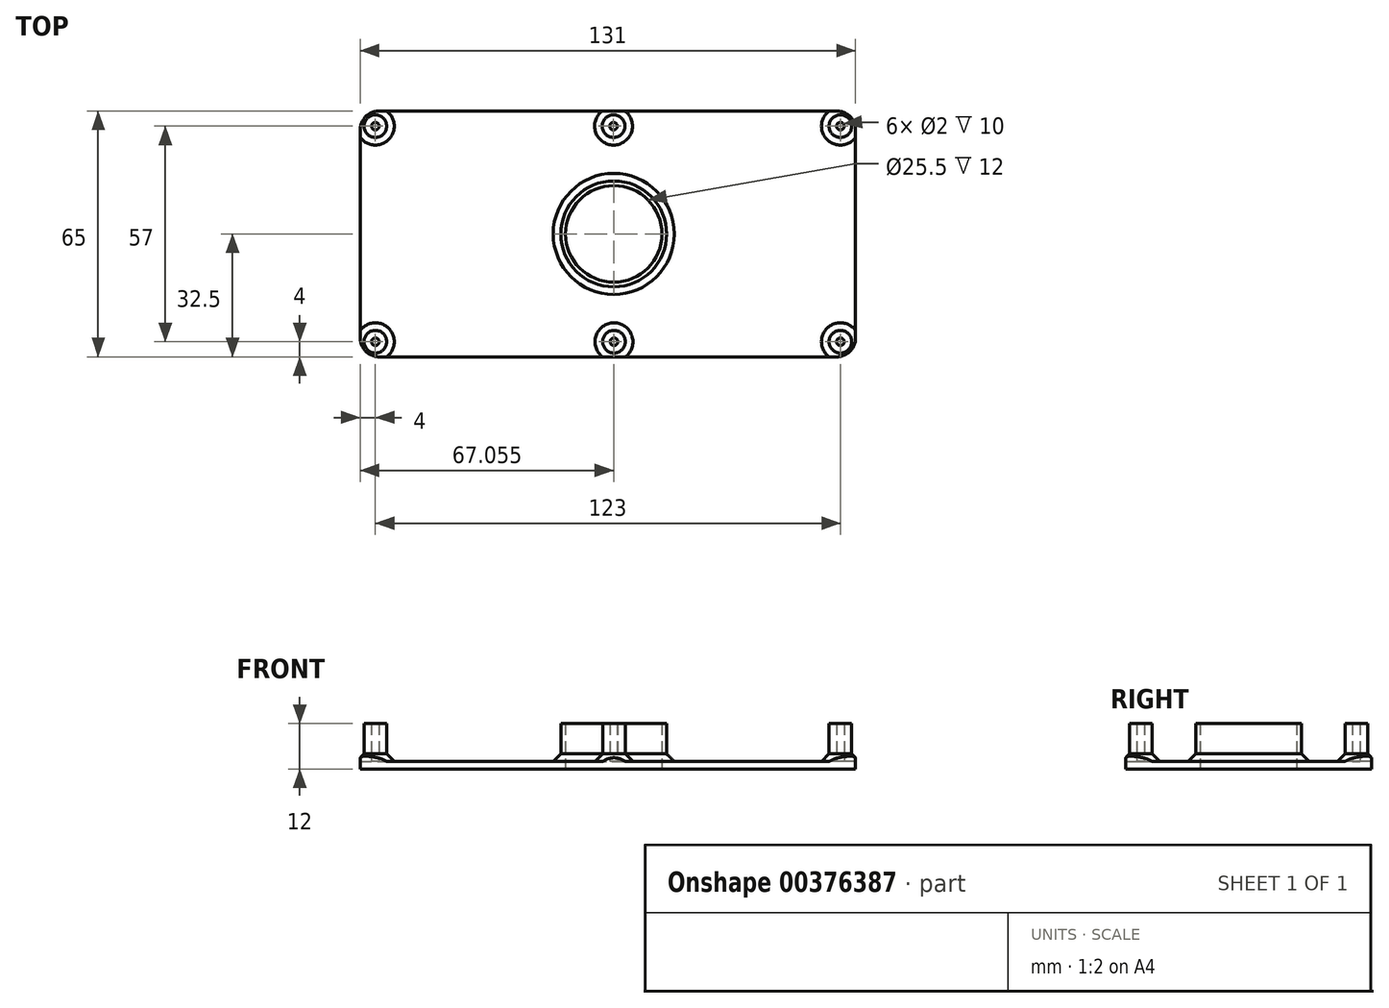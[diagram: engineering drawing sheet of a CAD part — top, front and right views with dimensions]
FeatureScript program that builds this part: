
annotation { "Feature Type Name" : "Feature", "Feature Type Description" : "" }
export const myFeature = defineFeature(function(context is Context, id is Id, definition is map)
    precondition{}
    {
        {
            var Q0;
            Q0=qCreatedBy(makeId("Top.planeOp"),FACE);
            var sketch = newSketch(context, id + "F0", { "sketchPlane" : qUnion([Q0])});
            skLineSegment(sketch, "E0.bottom", {"start": v(-65.5, 32.5) * mm, "end": v(65.5, 32.5) * mm});
            skLineSegment(sketch, "E0.top", {"start": v(-65.5, -32.5) * mm, "end": v(65.5, -32.5) * mm});
            skLineSegment(sketch, "E0.left", {"start": v(-65.5, 32.5) * mm, "end": v(-65.5, -32.5) * mm});
            skLineSegment(sketch, "E0.right", {"start": v(65.5, 32.5) * mm, "end": v(65.5, -32.5) * mm});
            skPoint(sketch, "E0.middle", {"position": v(0, 0) * mm});
            skLineSegment(sketch, "E1.bottom", {"start": v(-65.5, 32.5) * mm, "end": v(-61.5, 32.5) * mm, "construction": true});
            skLineSegment(sketch, "E1.top", {"start": v(-65.5, 28.5) * mm, "end": v(-61.5, 28.5) * mm, "construction": true});
            skLineSegment(sketch, "E1.left", {"start": v(-65.5, 32.5) * mm, "end": v(-65.5, 28.5) * mm, "construction": true});
            skLineSegment(sketch, "E1.right", {"start": v(-61.5, 32.5) * mm, "end": v(-61.5, 28.5) * mm, "construction": true});
            skLineSegment(sketch, "E2.bottom", {"start": v(65.5, 32.5) * mm, "end": v(61.5, 32.5) * mm, "construction": true});
            skLineSegment(sketch, "E2.top", {"start": v(65.5, 28.5) * mm, "end": v(61.5, 28.5) * mm, "construction": true});
            skLineSegment(sketch, "E2.left", {"start": v(65.5, 32.5) * mm, "end": v(65.5, 28.5) * mm, "construction": true});
            skLineSegment(sketch, "E2.right", {"start": v(61.5, 32.5) * mm, "end": v(61.5, 28.5) * mm, "construction": true});
            skLineSegment(sketch, "E3.bottom", {"start": v(-65.5, -32.5) * mm, "end": v(-61.5, -32.5) * mm, "construction": true});
            skLineSegment(sketch, "E3.top", {"start": v(-65.5, -28.5) * mm, "end": v(-61.5, -28.5) * mm, "construction": true});
            skLineSegment(sketch, "E3.left", {"start": v(-65.5, -32.5) * mm, "end": v(-65.5, -28.5) * mm, "construction": true});
            skLineSegment(sketch, "E3.right", {"start": v(-61.5, -32.5) * mm, "end": v(-61.5, -28.5) * mm, "construction": true});
            skLineSegment(sketch, "E4.bottom", {"start": v(65.5, -32.5) * mm, "end": v(61.5, -32.5) * mm, "construction": true});
            skLineSegment(sketch, "E4.top", {"start": v(65.5, -28.5) * mm, "end": v(61.5, -28.5) * mm, "construction": true});
            skLineSegment(sketch, "E4.left", {"start": v(65.5, -32.5) * mm, "end": v(65.5, -28.5) * mm, "construction": true});
            skLineSegment(sketch, "E4.right", {"start": v(61.5, -32.5) * mm, "end": v(61.5, -28.5) * mm, "construction": true});
            skCircle(sketch, "E5", {"center": v(-61.5, 28.5) * mm, "radius": 3 * mm});
            skCircle(sketch, "E6", {"center": v(-61.5, -28.5) * mm, "radius": 3 * mm});
            skCircle(sketch, "E7", {"center": v(61.5, -28.5) * mm, "radius": 3 * mm});
            skCircle(sketch, "E8", {"center": v(61.5, 28.5) * mm, "radius": 3 * mm});
            skLineSegment(sketch, "E9", {"start": v(65.5, 28.5) * mm, "end": v(1.5, 28.5) * mm, "construction": true});
            skPoint(sketch, "E9.endSnap0", {"position": v(63.5, 28.5) * mm});
            skLineSegment(sketch, "E10", {"start": v(65.5, -28.5) * mm, "end": v(1.61, -28.5) * mm});
            skLineSegment(sketch, "E11", {"start": v(1.5, 28.5) * mm, "end": v(1.5, 32.5) * mm, "construction": true});
            skLineSegment(sketch, "E12", {"start": v(1.61, -28.5) * mm, "end": v(1.61, -32.5) * mm, "construction": true});
            skCircle(sketch, "E13", {"center": v(1.5, 28.5) * mm, "radius": 3 * mm});
            skCircle(sketch, "E14", {"center": v(1.61, -28.5) * mm, "radius": 3 * mm});
            skLineSegment(sketch, "E15", {"start": v(1.5, 28.5) * mm, "end": v(1.61, -29.33) * mm, "construction": true});
            skCircle(sketch, "E16", {"center": v(1.55, 0) * mm, "radius": 14 * mm});
            skCircle(sketch, "E17", {"center": v(1.55, 0) * mm, "radius": 12.75 * mm});
            skSolve(sketch);
        }
        {
            var Q0;
            {var subQ7=sQuery(id+"F0.wireOp",EDGE,"E0.bottom");Q0=makeQuery(id+"F0.imprint","IMPRINT",FACE,{"disambiguationData":[TD([[makeQuery(id+"F0.imprint","IMPRINT",EDGE,{"derivedFrom":subQ7}),-1.0]])]});}
            var Q1;
            Q1=makeQuery(id+"F0.imprint","IMPRINT",FACE,{"disambiguationData":[TD([[makeQuery(id+"F0.imprint","IMPRINT",EDGE,{"derivedFrom":sQuery(id+"F0.wireOp",EDGE,"E13")}),1.0]])]});
            var Q2;
            Q2=makeQuery(id+"F0.imprint","IMPRINT",FACE,{"disambiguationData":[TD([[makeQuery(id+"F0.imprint","IMPRINT",EDGE,{"derivedFrom":sQuery(id+"F0.wireOp",EDGE,"E14")}),1.0]])]});
            var Q3;
            {var subQ0=sQuery(id+"F0.wireOp",EDGE,"E10");var subQ1=sQuery(id+"F0.wireOp",EDGE,"E7");var subQ2=makeQuery(id+"F0.imprint","INTERSECT",VERTEX,{"disambiguationData":[OD(0.0)],"derivedFrom":[subQ1,subQ0]});Q3=makeQuery(id+"F0.imprint","IMPRINT",FACE,{"disambiguationData":[TD([[makeQuery(id+"F0.imprint","IMPRINT",EDGE,{"disambiguationData":[TD([[subQ2,1.0]])],"derivedFrom":subQ1}),1.0]])]});}
            var Q4;
            {var subQ0=sQuery(id+"F0.wireOp",EDGE,"E10");var subQ1=sQuery(id+"F0.wireOp",EDGE,"E7");var subQ2=makeQuery(id+"F0.imprint","INTERSECT",VERTEX,{"disambiguationData":[OD(0.0)],"derivedFrom":[subQ1,subQ0]});Q4=makeQuery(id+"F0.imprint","IMPRINT",FACE,{"disambiguationData":[TD([[makeQuery(id+"F0.imprint","IMPRINT",EDGE,{"disambiguationData":[TD([[subQ2,-1.0]])],"derivedFrom":subQ1}),1.0]])]});}
            var Q5;
            Q5=makeQuery(id+"F0.imprint","IMPRINT",FACE,{"disambiguationData":[TD([[makeQuery(id+"F0.imprint","IMPRINT",EDGE,{"derivedFrom":sQuery(id+"F0.wireOp",EDGE,"E8")}),1.0]])]});
            var Q6;
            Q6=makeQuery(id+"F0.imprint","IMPRINT",FACE,{"disambiguationData":[TD([[makeQuery(id+"F0.imprint","IMPRINT",EDGE,{"derivedFrom":sQuery(id+"F0.wireOp",EDGE,"E6")}),1.0]])]});
            var Q7;
            Q7=makeQuery(id+"F0.imprint","IMPRINT",FACE,{"disambiguationData":[TD([[makeQuery(id+"F0.imprint","IMPRINT",EDGE,{"derivedFrom":sQuery(id+"F0.wireOp",EDGE,"E5")}),1.0]])]});
            var Q8;
            Q8=makeQuery(id+"F0.imprint","IMPRINT",FACE,{"disambiguationData":[TD([[makeQuery(id+"F0.imprint","IMPRINT",EDGE,{"derivedFrom":sQuery(id+"F0.wireOp",EDGE,"E16")}),1.0]])]});
            extrude(context, id + "F1", {"entities" : qUnion([Q0, Q1, Q2, Q3, Q4, Q5, Q6, Q7, Q8]), "depth" : 2 * mm});
        }
        {
            var Q0;
            Q0=makeQuery(id+"F0.imprint","IMPRINT",FACE,{"disambiguationData":[TD([[makeQuery(id+"F0.imprint","IMPRINT",EDGE,{"derivedFrom":sQuery(id+"F0.wireOp",EDGE,"E5")}),1.0]])]});
            var Q1;
            Q1=makeQuery(id+"F0.imprint","IMPRINT",FACE,{"disambiguationData":[TD([[makeQuery(id+"F0.imprint","IMPRINT",EDGE,{"derivedFrom":sQuery(id+"F0.wireOp",EDGE,"E6")}),1.0]])]});
            var Q2;
            Q2=makeQuery(id+"F0.imprint","IMPRINT",FACE,{"disambiguationData":[TD([[makeQuery(id+"F0.imprint","IMPRINT",EDGE,{"derivedFrom":sQuery(id+"F0.wireOp",EDGE,"E14")}),1.0]])]});
            var Q3;
            {var subQ0=sQuery(id+"F0.wireOp",EDGE,"E10");var subQ1=sQuery(id+"F0.wireOp",EDGE,"E7");var subQ2=makeQuery(id+"F0.imprint","INTERSECT",VERTEX,{"disambiguationData":[OD(0.0)],"derivedFrom":[subQ1,subQ0]});Q3=makeQuery(id+"F0.imprint","IMPRINT",FACE,{"disambiguationData":[TD([[makeQuery(id+"F0.imprint","IMPRINT",EDGE,{"disambiguationData":[TD([[subQ2,1.0]])],"derivedFrom":subQ1}),1.0]])]});}
            var Q4;
            {var subQ0=sQuery(id+"F0.wireOp",EDGE,"E10");var subQ1=sQuery(id+"F0.wireOp",EDGE,"E7");var subQ2=makeQuery(id+"F0.imprint","INTERSECT",VERTEX,{"disambiguationData":[OD(0.0)],"derivedFrom":[subQ1,subQ0]});Q4=makeQuery(id+"F0.imprint","IMPRINT",FACE,{"disambiguationData":[TD([[makeQuery(id+"F0.imprint","IMPRINT",EDGE,{"disambiguationData":[TD([[subQ2,-1.0]])],"derivedFrom":subQ1}),1.0]])]});}
            var Q5;
            Q5=makeQuery(id+"F0.imprint","IMPRINT",FACE,{"disambiguationData":[TD([[makeQuery(id+"F0.imprint","IMPRINT",EDGE,{"derivedFrom":sQuery(id+"F0.wireOp",EDGE,"E8")}),1.0]])]});
            var Q6;
            Q6=makeQuery(id+"F0.imprint","IMPRINT",FACE,{"disambiguationData":[TD([[makeQuery(id+"F0.imprint","IMPRINT",EDGE,{"derivedFrom":sQuery(id+"F0.wireOp",EDGE,"E13")}),1.0]])]});
            extrude(context, id + "F2", {"entities" : qUnion([Q0, Q1, Q2, Q3, Q4, Q5, Q6]), "operationType" : NewBodyOperationType.ADD, "depth" : 12 * mm});
        }
        {
            var Q0;
            Q0=makeQuery(id+"F2.opExtrude","CAP_FACE",FACE,{"disambiguationData":[OSD([sQuery(id+"F0.wireOp",EDGE,"E5")])],"isStart":false});
            var Q1;
            Q1=makeQuery(id+"F2.opExtrude","CAP_FACE",FACE,{"disambiguationData":[OSD([sQuery(id+"F0.wireOp",EDGE,"E13")])],"isStart":false});
            var Q2;
            Q2=makeQuery(id+"F2.opExtrude","CAP_FACE",FACE,{"disambiguationData":[OSD([sQuery(id+"F0.wireOp",EDGE,"E8")])],"isStart":false});
            var Q3;
            Q3=makeQuery(id+"F2.opExtrude","CAP_FACE",FACE,{"disambiguationData":[OSD([sQuery(id+"F0.wireOp",EDGE,"E7")])],"isStart":false});
            var Q4;
            Q4=makeQuery(id+"F2.opExtrude","CAP_FACE",FACE,{"disambiguationData":[OSD([sQuery(id+"F0.wireOp",EDGE,"E14")])],"isStart":false});
            var Q5;
            Q5=makeQuery(id+"F2.opExtrude","CAP_FACE",FACE,{"disambiguationData":[OSD([sQuery(id+"F0.wireOp",EDGE,"E6")])],"isStart":false});
            shell(context, id + "F3", {"entities" : qUnion([Q0, Q1, Q2, Q3, Q4, Q5]), "thickness" : 2 * mm});
        }
        {
            var Q0;
            Q0=makeQuery(id+"F0.imprint","IMPRINT",FACE,{"disambiguationData":[TD([[makeQuery(id+"F0.imprint","IMPRINT",EDGE,{"derivedFrom":sQuery(id+"F0.wireOp",EDGE,"E16")}),1.0]])]});
            extrude(context, id + "F4", {"entities" : qUnion([Q0]), "operationType" : NewBodyOperationType.ADD, "depth" : 12 * mm});
        }
        {
            var Q0;
            Q0=makeQuery(id+"F1.opExtrude","SWEPT_EDGE",EDGE,{"disambiguationData":[OSD([sQuery(id+"F0.wireOp",EDGE,"E0.top"),sQuery(id+"F0.wireOp",EDGE,"E0.right")])]});
            var Q1;
            Q1=makeQuery(id+"F1.opExtrude","SWEPT_EDGE",EDGE,{"disambiguationData":[OSD([sQuery(id+"F0.wireOp",EDGE,"E0.top"),sQuery(id+"F0.wireOp",EDGE,"E0.left")])]});
            var Q2;
            Q2=makeQuery(id+"F1.opExtrude","SWEPT_EDGE",EDGE,{"disambiguationData":[OSD([sQuery(id+"F0.wireOp",EDGE,"E0.bottom"),sQuery(id+"F0.wireOp",EDGE,"E0.right")])]});
            var Q3;
            Q3=makeQuery(id+"F1.opExtrude","SWEPT_EDGE",EDGE,{"disambiguationData":[OSD([sQuery(id+"F0.wireOp",EDGE,"E0.bottom"),sQuery(id+"F0.wireOp",EDGE,"E0.left")])]});
            fillet(context, id + "F5", {"entities" : qUnion([Q0, Q1, Q2, Q3]), "radius" : 5 * mm, "tangentPropagation" : true, "allowEdgeOverflow" : false});
        }
        {
            var Q0;
            Q0=makeQuery(id+"F4.boolean.opBoolean","INTERSECT",EDGE,{"derivedFrom":[makeQuery(id+"F1.opExtrude","CAP_FACE",FACE,{"disambiguationData":[OSD([sQuery(id+"F0.wireOp",EDGE,"E0.bottom"),sQuery(id+"F0.wireOp",EDGE,"E0.top"),sQuery(id+"F0.wireOp",EDGE,"E0.left"),sQuery(id+"F0.wireOp",EDGE,"E0.right"),sQuery(id+"F0.wireOp",EDGE,"E17")])],"isStart":false}),makeQuery(id+"F4.opExtrude","SWEPT_FACE",FACE,{"disambiguationData":[OSD([sQuery(id+"F0.wireOp",EDGE,"E16")])]})]});
            var Q1;
            Q1=makeQuery(id+"F2.boolean.opBoolean","INTERSECT",EDGE,{"derivedFrom":[makeQuery(id+"F1.opExtrude","CAP_FACE",FACE,{"disambiguationData":[OSD([sQuery(id+"F0.wireOp",EDGE,"E0.bottom"),sQuery(id+"F0.wireOp",EDGE,"E0.top"),sQuery(id+"F0.wireOp",EDGE,"E0.left"),sQuery(id+"F0.wireOp",EDGE,"E0.right"),sQuery(id+"F0.wireOp",EDGE,"E17")])],"isStart":false}),makeQuery(id+"F2.opExtrude","SWEPT_FACE",FACE,{"disambiguationData":[OSD([sQuery(id+"F0.wireOp",EDGE,"E14")])]})]});
            var Q2;
            Q2=makeQuery(id+"F2.boolean.opBoolean","INTERSECT",EDGE,{"derivedFrom":[makeQuery(id+"F1.opExtrude","CAP_FACE",FACE,{"disambiguationData":[OSD([sQuery(id+"F0.wireOp",EDGE,"E0.bottom"),sQuery(id+"F0.wireOp",EDGE,"E0.top"),sQuery(id+"F0.wireOp",EDGE,"E0.left"),sQuery(id+"F0.wireOp",EDGE,"E0.right"),sQuery(id+"F0.wireOp",EDGE,"E17")])],"isStart":false}),makeQuery(id+"F2.opExtrude","SWEPT_FACE",FACE,{"disambiguationData":[OSD([sQuery(id+"F0.wireOp",EDGE,"E6")])]})]});
            var Q3;
            Q3=makeQuery(id+"F2.boolean.opBoolean","INTERSECT",EDGE,{"derivedFrom":[makeQuery(id+"F1.opExtrude","CAP_FACE",FACE,{"disambiguationData":[OSD([sQuery(id+"F0.wireOp",EDGE,"E0.bottom"),sQuery(id+"F0.wireOp",EDGE,"E0.top"),sQuery(id+"F0.wireOp",EDGE,"E0.left"),sQuery(id+"F0.wireOp",EDGE,"E0.right"),sQuery(id+"F0.wireOp",EDGE,"E17")])],"isStart":false}),makeQuery(id+"F2.opExtrude","SWEPT_FACE",FACE,{"disambiguationData":[OSD([sQuery(id+"F0.wireOp",EDGE,"E7")])]})]});
            var Q4;
            Q4=makeQuery(id+"F2.boolean.opBoolean","INTERSECT",EDGE,{"derivedFrom":[makeQuery(id+"F1.opExtrude","CAP_FACE",FACE,{"disambiguationData":[OSD([sQuery(id+"F0.wireOp",EDGE,"E0.bottom"),sQuery(id+"F0.wireOp",EDGE,"E0.top"),sQuery(id+"F0.wireOp",EDGE,"E0.left"),sQuery(id+"F0.wireOp",EDGE,"E0.right"),sQuery(id+"F0.wireOp",EDGE,"E17")])],"isStart":false}),makeQuery(id+"F2.opExtrude","SWEPT_FACE",FACE,{"disambiguationData":[OSD([sQuery(id+"F0.wireOp",EDGE,"E8")])]})]});
            var Q5;
            Q5=makeQuery(id+"F2.boolean.opBoolean","INTERSECT",EDGE,{"derivedFrom":[makeQuery(id+"F1.opExtrude","CAP_FACE",FACE,{"disambiguationData":[OSD([sQuery(id+"F0.wireOp",EDGE,"E0.bottom"),sQuery(id+"F0.wireOp",EDGE,"E0.top"),sQuery(id+"F0.wireOp",EDGE,"E0.left"),sQuery(id+"F0.wireOp",EDGE,"E0.right"),sQuery(id+"F0.wireOp",EDGE,"E17")])],"isStart":false}),makeQuery(id+"F2.opExtrude","SWEPT_FACE",FACE,{"disambiguationData":[OSD([sQuery(id+"F0.wireOp",EDGE,"E13")])]})]});
            var Q6;
            Q6=makeQuery(id+"F2.boolean.opBoolean","INTERSECT",EDGE,{"derivedFrom":[makeQuery(id+"F1.opExtrude","CAP_FACE",FACE,{"disambiguationData":[OSD([sQuery(id+"F0.wireOp",EDGE,"E0.bottom"),sQuery(id+"F0.wireOp",EDGE,"E0.top"),sQuery(id+"F0.wireOp",EDGE,"E0.left"),sQuery(id+"F0.wireOp",EDGE,"E0.right"),sQuery(id+"F0.wireOp",EDGE,"E17")])],"isStart":false}),makeQuery(id+"F2.opExtrude","SWEPT_FACE",FACE,{"disambiguationData":[OSD([sQuery(id+"F0.wireOp",EDGE,"E5")])]})]});
            chamfer(context, id + "F6", {"entities" : qUnion([Q0, Q1, Q2, Q3, Q4, Q5, Q6]), "width" : 2 * mm, "tangentPropagation" : true});
        }
    });
